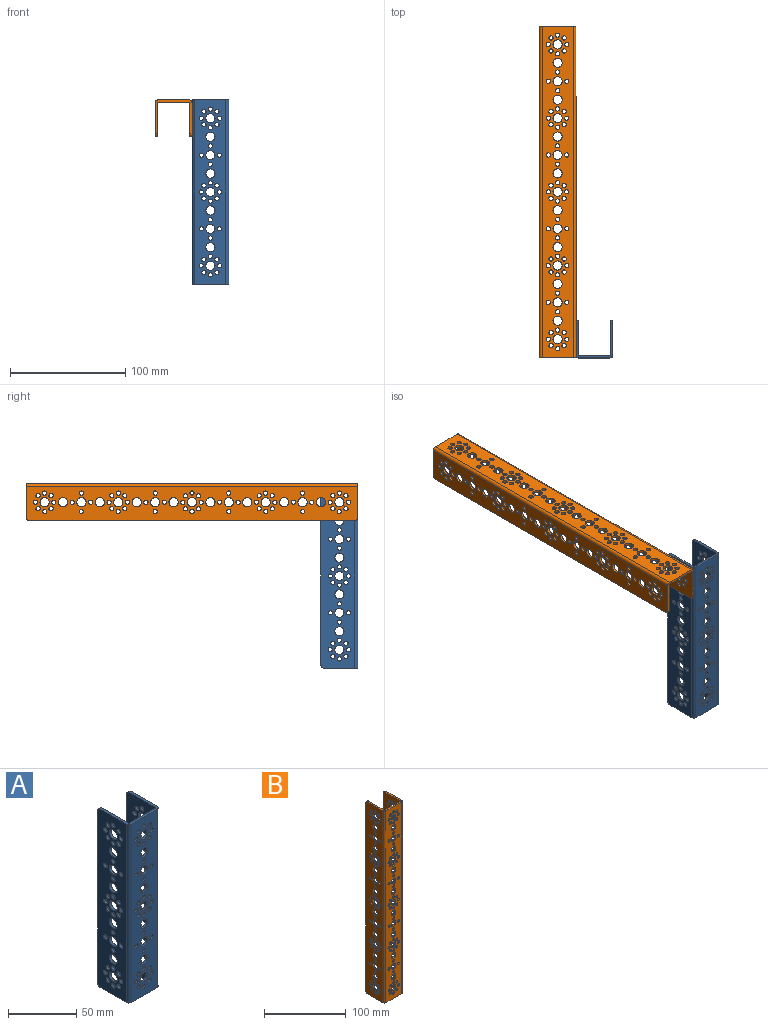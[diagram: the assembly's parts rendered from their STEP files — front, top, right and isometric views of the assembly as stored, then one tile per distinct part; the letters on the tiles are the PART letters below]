
ASSEMBLY  parts=2 mates=1
PART A: 141 faces, bbox 32x32x160 mm
  f0: cylinder r=2.5mm len=160mm, axis (0,0,-1), area 628.3mm2, adj f1,f11,f12,f13
  f1: plane 160x27mm, normal (0,-1,0), area 3523.5mm2, adj f0,f2,f12,f13,f18,f23,f24,f25
  f2: cylinder r=2.5mm len=160mm, axis (0,0,-1), area 628.3mm2, adj f1,f3,f12,f13
  f3: plane 160x29.5mm, normal (1,0,0), area 3920.9mm2, adj f2,f4,f12,f13,f14,f17,f20,f22
  f4: plane 155x2mm, normal (0,1,0), area 310mm2, adj f3,f5,f14,f17
  f5: plane 160x29.5mm, normal (-1,0,0), area 3920.9mm2, adj f4,f6,f12,f13,f14,f17,f20,f22
  f6: cylinder r=0.5mm len=160mm, axis (0,0,-1), area 125.7mm2, adj f5,f7,f12,f13
  f7: plane 160x27mm, normal (0,1,0), area 3523.5mm2, adj f6,f8,f12,f13,f18,f23,f24,f25
  f8: cylinder r=0.5mm len=160mm, axis (0,0,-1), area 125.7mm2, adj f7,f9,f12,f13
  f9: plane 160x29.5mm, normal (1,0,0), area 3920.9mm2, adj f8,f10,f12,f13,f15,f16,f19,f21
  f10: plane 155x2mm, normal (0,1,0), area 310mm2, adj f9,f11,f15,f16
  f11: plane 160x29.5mm, normal (-1,0,0), area 3920.9mm2, adj f0,f10,f12,f13,f15,f16,f19,f21
  f12: plane 32x29.5mm, normal (0,0,1), area 171.4mm2, adj f0,f1,f2,f3,f5,f6,f7,f8
  f13: plane 32x29.5mm, normal (0,0,-1), area 171.4mm2, adj f0,f1,f2,f3,f5,f6,f7,f8
  f14: cylinder r=2.5mm len=2.5mm, axis (1,0,0), area 7.9mm2, adj f3,f4,f5,f12
  f15: cylinder r=2.5mm len=2.5mm, axis (1,0,0), area 7.9mm2, adj f9,f10,f11,f12
  f16: cylinder r=2.5mm len=2.5mm, axis (-1,0,0), area 7.9mm2, adj f9,f10,f11,f13
  f17: cylinder r=2.5mm len=2.5mm, axis (-1,0,0), area 7.9mm2, adj f3,f4,f5,f13
  f18: cylinder r=4mm len=8mm, axis (0,-1,0), area 50.3mm2, adj f1,f7
  f19: cylinder r=4mm len=8mm, axis (-1,0,0), area 50.3mm2, adj f9,f11
  f20: cylinder r=4mm len=8mm, axis (-1,0,0), area 50.3mm2, adj f3,f5
  f21: cylinder r=1.85mm len=3.7mm, axis (-1,0,0), area 23.2mm2, adj f9,f11
  f22: cylinder r=1.85mm len=3.7mm, axis (-1,0,0), area 23.2mm2, adj f3,f5
  f23: cylinder r=1.85mm len=3.7mm, axis (0,-1,0), area 23.2mm2, adj f1,f7
  f24: cylinder r=4mm len=8mm, axis (0,-1,0), area 50.3mm2, adj f1,f7
  f25: cylinder r=4mm len=8mm, axis (0,-1,0), area 50.3mm2, adj f1,f7
  f26: cylinder r=4mm len=8mm, axis (0,-1,0), area 50.3mm2, adj f1,f7
  f27: cylinder r=4mm len=8mm, axis (0,-1,0), area 50.3mm2, adj f1,f7
  f28: cylinder r=4mm len=8mm, axis (0,-1,0), area 50.3mm2, adj f1,f7
  f29: cylinder r=4mm len=8mm, axis (0,-1,0), area 50.3mm2, adj f1,f7
  f30: cylinder r=4mm len=8mm, axis (0,-1,0), area 50.3mm2, adj f1,f7
  f31: cylinder r=4mm len=8mm, axis (0,-1,0), area 50.3mm2, adj f1,f7
  f32: cylinder r=4mm len=8mm, axis (-1,0,0), area 50.3mm2, adj f9,f11
  f33: cylinder r=4mm len=8mm, axis (-1,0,0), area 50.3mm2, adj f3,f5
  f34: cylinder r=4mm len=8mm, axis (-1,0,0), area 50.3mm2, adj f9,f11
  f35: cylinder r=4mm len=8mm, axis (-1,0,0), area 50.3mm2, adj f3,f5
  f36: cylinder r=4mm len=8mm, axis (-1,0,0), area 50.3mm2, adj f9,f11
  f37: cylinder r=4mm len=8mm, axis (-1,0,0), area 50.3mm2, adj f3,f5
  f38: cylinder r=4mm len=8mm, axis (-1,0,0), area 50.3mm2, adj f9,f11
  f39: cylinder r=4mm len=8mm, axis (-1,0,0), area 50.3mm2, adj f3,f5
  f40: cylinder r=4mm len=8mm, axis (-1,0,0), area 50.3mm2, adj f9,f11
  f41: cylinder r=4mm len=8mm, axis (-1,0,0), area 50.3mm2, adj f3,f5
  f42: cylinder r=4mm len=8mm, axis (-1,0,0), area 50.3mm2, adj f9,f11
  f43: cylinder r=4mm len=8mm, axis (-1,0,0), area 50.3mm2, adj f3,f5
  f44: cylinder r=4mm len=8mm, axis (-1,0,0), area 50.3mm2, adj f9,f11
  f45: cylinder r=4mm len=8mm, axis (-1,0,0), area 50.3mm2, adj f3,f5
  f46: cylinder r=4mm len=8mm, axis (-1,0,0), area 50.3mm2, adj f9,f11
  f47: cylinder r=4mm len=8mm, axis (-1,0,0), area 50.3mm2, adj f3,f5
  f48: cylinder r=1.85mm len=3.7mm, axis (0,-1,0), area 23.2mm2, adj f1,f7
  f49: cylinder r=1.85mm len=3.7mm, axis (0,-1,0), area 23.2mm2, adj f1,f7
  f50: cylinder r=1.85mm len=3.7mm, axis (0,-1,0), area 23.2mm2, adj f1,f7
  f51: cylinder r=1.85mm len=3.7mm, axis (0,-1,0), area 23.2mm2, adj f1,f7
  f52: cylinder r=1.85mm len=3.7mm, axis (0,-1,0), area 23.2mm2, adj f1,f7
  f53: cylinder r=1.85mm len=3.7mm, axis (0,-1,0), area 23.2mm2, adj f1,f7
  f54: cylinder r=1.85mm len=3.7mm, axis (0,-1,0), area 23.2mm2, adj f1,f7
  f55: cylinder r=1.85mm len=3.7mm, axis (-1,0,0), area 23.2mm2, adj f9,f11
  f56: cylinder r=1.85mm len=3.7mm, axis (-1,0,0), area 23.2mm2, adj f3,f5
  f57: cylinder r=1.85mm len=3.7mm, axis (-1,0,0), area 23.2mm2, adj f9,f11
  f58: cylinder r=1.85mm len=3.7mm, axis (-1,0,0), area 23.2mm2, adj f3,f5
  f59: cylinder r=1.85mm len=3.7mm, axis (-1,0,0), area 23.2mm2, adj f9,f11
  f60: cylinder r=1.85mm len=3.7mm, axis (-1,0,0), area 23.2mm2, adj f3,f5
  f61: cylinder r=1.85mm len=3.7mm, axis (-1,0,0), area 23.2mm2, adj f9,f11
  f62: cylinder r=1.85mm len=3.7mm, axis (-1,0,0), area 23.2mm2, adj f3,f5
  f63: cylinder r=1.85mm len=3.7mm, axis (-1,0,0), area 23.2mm2, adj f9,f11
  f64: cylinder r=1.85mm len=3.7mm, axis (-1,0,0), area 23.2mm2, adj f3,f5
  f65: cylinder r=1.85mm len=3.7mm, axis (-1,0,0), area 23.2mm2, adj f9,f11
  f66: cylinder r=1.85mm len=3.7mm, axis (-1,0,0), area 23.2mm2, adj f3,f5
  f67: cylinder r=1.85mm len=3.7mm, axis (-1,0,0), area 23.2mm2, adj f9,f11
  f68: cylinder r=1.85mm len=3.7mm, axis (-1,0,0), area 23.2mm2, adj f3,f5
  f69: cylinder r=1.85mm len=3.7mm, axis (0,-1,0), area 23.2mm2, adj f1,f7
  f70: cylinder r=1.85mm len=3.7mm, axis (-1,0,0), area 23.2mm2, adj f9,f11
  f71: cylinder r=1.85mm len=3.7mm, axis (-1,0,0), area 23.2mm2, adj f3,f5
  f72: cylinder r=1.85mm len=3.7mm, axis (0,-1,0), area 23.2mm2, adj f1,f7
  f73: cylinder r=1.85mm len=3.7mm, axis (0,-1,0), area 23.2mm2, adj f1,f7
  f74: cylinder r=1.85mm len=3.7mm, axis (0,-1,0), area 23.2mm2, adj f1,f7
  f75: cylinder r=1.85mm len=3.7mm, axis (-1,0,0), area 23.2mm2, adj f9,f11
  f76: cylinder r=1.85mm len=3.7mm, axis (-1,0,0), area 23.2mm2, adj f3,f5
  f77: cylinder r=1.85mm len=3.7mm, axis (-1,0,0), area 23.2mm2, adj f9,f11
  f78: cylinder r=1.85mm len=3.7mm, axis (-1,0,0), area 23.2mm2, adj f3,f5
  f79: cylinder r=1.85mm len=3.7mm, axis (-1,0,0), area 23.2mm2, adj f9,f11
  f80: cylinder r=1.85mm len=3.7mm, axis (-1,0,0), area 23.2mm2, adj f3,f5
  f81: cylinder r=1.85mm len=3.7mm, axis (0,-1,0), area 23.2mm2, adj f1,f7
  f82: cylinder r=1.85mm len=3.7mm, axis (0,-1,0), area 23.2mm2, adj f1,f7
  f83: cylinder r=1.85mm len=3.7mm, axis (0,-1,0), area 23.2mm2, adj f1,f7
  f84: cylinder r=1.85mm len=3.7mm, axis (0,-1,0), area 23.2mm2, adj f1,f7
  f85: cylinder r=1.85mm len=3.7mm, axis (0,-1,0), area 23.2mm2, adj f1,f7
  f86: cylinder r=1.85mm len=3.7mm, axis (0,-1,0), area 23.2mm2, adj f1,f7
  f87: cylinder r=1.85mm len=3.7mm, axis (0,-1,0), area 23.2mm2, adj f1,f7
  f88: cylinder r=1.85mm len=3.7mm, axis (0,-1,0), area 23.2mm2, adj f1,f7
  f89: cylinder r=1.85mm len=3.7mm, axis (-1,0,0), area 23.2mm2, adj f9,f11
  f90: cylinder r=1.85mm len=3.7mm, axis (-1,0,0), area 23.2mm2, adj f3,f5
  f91: cylinder r=1.85mm len=3.7mm, axis (-1,0,0), area 23.2mm2, adj f9,f11
  f92: cylinder r=1.85mm len=3.7mm, axis (-1,0,0), area 23.2mm2, adj f3,f5
  f93: cylinder r=1.85mm len=3.7mm, axis (-1,0,0), area 23.2mm2, adj f9,f11
  f94: cylinder r=1.85mm len=3.7mm, axis (-1,0,0), area 23.2mm2, adj f3,f5
  f95: cylinder r=1.85mm len=3.7mm, axis (-1,0,0), area 23.2mm2, adj f9,f11
  f96: cylinder r=1.85mm len=3.7mm, axis (-1,0,0), area 23.2mm2, adj f3,f5
  f97: cylinder r=1.85mm len=3.7mm, axis (-1,0,0), area 23.2mm2, adj f9,f11
  f98: cylinder r=1.85mm len=3.7mm, axis (-1,0,0), area 23.2mm2, adj f3,f5
  f99: cylinder r=1.85mm len=3.7mm, axis (-1,0,0), area 23.2mm2, adj f9,f11
  f100: cylinder r=1.85mm len=3.7mm, axis (-1,0,0), area 23.2mm2, adj f3,f5
  f101: cylinder r=1.85mm len=3.7mm, axis (-1,0,0), area 23.2mm2, adj f9,f11
  f102: cylinder r=1.85mm len=3.7mm, axis (-1,0,0), area 23.2mm2, adj f3,f5
  f103: cylinder r=1.85mm len=3.7mm, axis (-1,0,0), area 23.2mm2, adj f9,f11
  f104: cylinder r=1.85mm len=3.7mm, axis (-1,0,0), area 23.2mm2, adj f3,f5
  f105: cylinder r=1.85mm len=3.7mm, axis (0,-1,0), area 23.2mm2, adj f1,f7
  f106: cylinder r=1.85mm len=3.7mm, axis (0,-1,0), area 23.2mm2, adj f1,f7
  f107: cylinder r=1.85mm len=3.7mm, axis (0,-1,0), area 23.2mm2, adj f1,f7
  f108: cylinder r=1.85mm len=3.7mm, axis (0,-1,0), area 23.2mm2, adj f1,f7
  f109: cylinder r=1.85mm len=3.7mm, axis (-1,0,0), area 23.2mm2, adj f3,f5
  f110: cylinder r=1.85mm len=3.7mm, axis (-1,0,0), area 23.2mm2, adj f3,f5
  f111: cylinder r=1.85mm len=3.7mm, axis (-1,0,0), area 23.2mm2, adj f3,f5
  f112: cylinder r=1.85mm len=3.7mm, axis (-1,0,0), area 23.2mm2, adj f3,f5
  f113: cylinder r=1.85mm len=3.7mm, axis (-1,0,0), area 23.2mm2, adj f9,f11
  f114: cylinder r=1.85mm len=3.7mm, axis (-1,0,0), area 23.2mm2, adj f9,f11
  f115: cylinder r=1.85mm len=3.7mm, axis (-1,0,0), area 23.2mm2, adj f9,f11
  f116: cylinder r=1.85mm len=3.7mm, axis (-1,0,0), area 23.2mm2, adj f9,f11
  f117: cylinder r=1.85mm len=3.7mm, axis (-1,0,0), area 23.2mm2, adj f3,f5
  f118: cylinder r=1.85mm len=3.7mm, axis (-1,0,0), area 23.2mm2, adj f3,f5
  f119: cylinder r=1.85mm len=3.7mm, axis (-1,0,0), area 23.2mm2, adj f3,f5
  f120: cylinder r=1.85mm len=3.7mm, axis (-1,0,0), area 23.2mm2, adj f3,f5
  f121: cylinder r=1.85mm len=3.7mm, axis (-1,0,0), area 23.2mm2, adj f3,f5
  f122: cylinder r=1.85mm len=3.7mm, axis (-1,0,0), area 23.2mm2, adj f3,f5
  f123: cylinder r=1.85mm len=3.7mm, axis (-1,0,0), area 23.2mm2, adj f3,f5
  f124: cylinder r=1.85mm len=3.7mm, axis (-1,0,0), area 23.2mm2, adj f3,f5
  f125: cylinder r=1.85mm len=3.7mm, axis (-1,0,0), area 23.2mm2, adj f9,f11
  f126: cylinder r=1.85mm len=3.7mm, axis (-1,0,0), area 23.2mm2, adj f9,f11
  f127: cylinder r=1.85mm len=3.7mm, axis (-1,0,0), area 23.2mm2, adj f9,f11
  f128: cylinder r=1.85mm len=3.7mm, axis (-1,0,0), area 23.2mm2, adj f9,f11
  f129: cylinder r=1.85mm len=3.7mm, axis (-1,0,0), area 23.2mm2, adj f9,f11
  f130: cylinder r=1.85mm len=3.7mm, axis (-1,0,0), area 23.2mm2, adj f9,f11
  f131: cylinder r=1.85mm len=3.7mm, axis (-1,0,0), area 23.2mm2, adj f9,f11
  f132: cylinder r=1.85mm len=3.7mm, axis (-1,0,0), area 23.2mm2, adj f9,f11
  f133: cylinder r=1.85mm len=3.7mm, axis (0,-1,0), area 23.2mm2, adj f1,f7
  f134: cylinder r=1.85mm len=3.7mm, axis (0,-1,0), area 23.2mm2, adj f1,f7
  f135: cylinder r=1.85mm len=3.7mm, axis (0,-1,0), area 23.2mm2, adj f1,f7
  f136: cylinder r=1.85mm len=3.7mm, axis (0,-1,0), area 23.2mm2, adj f1,f7
  f137: cylinder r=1.85mm len=3.7mm, axis (0,-1,0), area 23.2mm2, adj f1,f7
  f138: cylinder r=1.85mm len=3.7mm, axis (0,-1,0), area 23.2mm2, adj f1,f7
  f139: cylinder r=1.85mm len=3.7mm, axis (0,-1,0), area 23.2mm2, adj f1,f7
  f140: cylinder r=1.85mm len=3.7mm, axis (0,-1,0), area 23.2mm2, adj f1,f7
PART B: 237 faces, bbox 32x32x288 mm
  f0: plane 288x29.5mm, normal (1,0,0), area 7036.7mm2, adj f7,f8,f12,f13,f14,f17,f20,f22
  f1: plane 288x29.5mm, normal (-1,0,0), area 7036.7mm2, adj f8,f9,f12,f13,f14,f17,f20,f22
  f2: plane 288x29.5mm, normal (1,0,0), area 7036.7mm2, adj f10,f11,f12,f13,f15,f16,f19,f21
  f3: plane 288x29.5mm, normal (-1,0,0), area 7036.7mm2, adj f6,f11,f12,f13,f15,f16,f19,f21
  f4: plane 288x27mm, normal (0,-1,0), area 6319.4mm2, adj f6,f7,f12,f13,f18,f23,f24,f25
  f5: plane 288x27mm, normal (0,1,0), area 6319.4mm2, adj f9,f10,f12,f13,f18,f23,f24,f25
  f6: cylinder r=2.5mm len=288mm, axis (0,0,-1), area 1131mm2, adj f3,f4,f12,f13
  f7: cylinder r=2.5mm len=288mm, axis (0,0,-1), area 1131mm2, adj f0,f4,f12,f13
  f8: plane 283x2mm, normal (0,1,0), area 566mm2, adj f0,f1,f14,f17
  f9: cylinder r=0.5mm len=288mm, axis (0,0,-1), area 226.2mm2, adj f1,f5,f12,f13
  f10: cylinder r=0.5mm len=288mm, axis (0,0,-1), area 226.2mm2, adj f2,f5,f12,f13
  f11: plane 283x2mm, normal (0,1,0), area 566mm2, adj f2,f3,f15,f16
  f12: plane 32x29.5mm, normal (0,0,1), area 171.4mm2, adj f0,f1,f2,f3,f4,f5,f6,f7
  f13: plane 32x29.5mm, normal (0,0,-1), area 171.4mm2, adj f0,f1,f2,f3,f4,f5,f6,f7
  f14: cylinder r=2.5mm len=2.5mm, axis (1,0,0), area 7.9mm2, adj f0,f1,f8,f12
  f15: cylinder r=2.5mm len=2.5mm, axis (1,0,0), area 7.9mm2, adj f2,f3,f11,f12
  f16: cylinder r=2.5mm len=2.5mm, axis (-1,0,0), area 7.9mm2, adj f2,f3,f11,f13
  f17: cylinder r=2.5mm len=2.5mm, axis (-1,0,0), area 7.9mm2, adj f0,f1,f8,f13
  f18: cylinder r=4mm len=8mm, axis (0,-1,0), area 50.3mm2, adj f4,f5
  f19: cylinder r=4mm len=8mm, axis (-1,0,0), area 50.3mm2, adj f2,f3
  f20: cylinder r=4mm len=8mm, axis (-1,0,0), area 50.3mm2, adj f0,f1
  f21: cylinder r=1.85mm len=3.7mm, axis (-1,0,0), area 23.2mm2, adj f2,f3
  f22: cylinder r=1.85mm len=3.7mm, axis (-1,0,0), area 23.2mm2, adj f0,f1
  f23: cylinder r=1.85mm len=3.7mm, axis (0,-1,0), area 23.2mm2, adj f4,f5
  f24: cylinder r=4mm len=8mm, axis (0,-1,0), area 50.3mm2, adj f4,f5
  f25: cylinder r=4mm len=8mm, axis (0,-1,0), area 50.3mm2, adj f4,f5
  f26: cylinder r=4mm len=8mm, axis (0,-1,0), area 50.3mm2, adj f4,f5
  f27: cylinder r=4mm len=8mm, axis (0,-1,0), area 50.3mm2, adj f4,f5
  f28: cylinder r=4mm len=8mm, axis (0,-1,0), area 50.3mm2, adj f4,f5
  f29: cylinder r=4mm len=8mm, axis (0,-1,0), area 50.3mm2, adj f4,f5
  f30: cylinder r=4mm len=8mm, axis (0,-1,0), area 50.3mm2, adj f4,f5
  f31: cylinder r=4mm len=8mm, axis (0,-1,0), area 50.3mm2, adj f4,f5
  f32: cylinder r=4mm len=8mm, axis (0,-1,0), area 50.3mm2, adj f4,f5
  f33: cylinder r=4mm len=8mm, axis (0,-1,0), area 50.3mm2, adj f4,f5
  f34: cylinder r=4mm len=8mm, axis (0,-1,0), area 50.3mm2, adj f4,f5
  f35: cylinder r=4mm len=8mm, axis (0,-1,0), area 50.3mm2, adj f4,f5
  f36: cylinder r=4mm len=8mm, axis (0,-1,0), area 50.3mm2, adj f4,f5
  f37: cylinder r=4mm len=8mm, axis (0,-1,0), area 50.3mm2, adj f4,f5
  f38: cylinder r=4mm len=8mm, axis (0,-1,0), area 50.3mm2, adj f4,f5
  f39: cylinder r=4mm len=8mm, axis (0,-1,0), area 50.3mm2, adj f4,f5
  f40: cylinder r=4mm len=8mm, axis (-1,0,0), area 50.3mm2, adj f2,f3
  f41: cylinder r=4mm len=8mm, axis (-1,0,0), area 50.3mm2, adj f0,f1
  f42: cylinder r=4mm len=8mm, axis (-1,0,0), area 50.3mm2, adj f2,f3
  f43: cylinder r=4mm len=8mm, axis (-1,0,0), area 50.3mm2, adj f0,f1
  f44: cylinder r=4mm len=8mm, axis (-1,0,0), area 50.3mm2, adj f2,f3
  f45: cylinder r=4mm len=8mm, axis (-1,0,0), area 50.3mm2, adj f0,f1
  f46: cylinder r=4mm len=8mm, axis (-1,0,0), area 50.3mm2, adj f2,f3
  f47: cylinder r=4mm len=8mm, axis (-1,0,0), area 50.3mm2, adj f0,f1
  f48: cylinder r=4mm len=8mm, axis (-1,0,0), area 50.3mm2, adj f2,f3
  f49: cylinder r=4mm len=8mm, axis (-1,0,0), area 50.3mm2, adj f0,f1
  f50: cylinder r=4mm len=8mm, axis (-1,0,0), area 50.3mm2, adj f2,f3
  f51: cylinder r=4mm len=8mm, axis (-1,0,0), area 50.3mm2, adj f0,f1
  f52: cylinder r=4mm len=8mm, axis (-1,0,0), area 50.3mm2, adj f2,f3
  f53: cylinder r=4mm len=8mm, axis (-1,0,0), area 50.3mm2, adj f0,f1
  f54: cylinder r=4mm len=8mm, axis (-1,0,0), area 50.3mm2, adj f2,f3
  f55: cylinder r=4mm len=8mm, axis (-1,0,0), area 50.3mm2, adj f0,f1
  f56: cylinder r=4mm len=8mm, axis (-1,0,0), area 50.3mm2, adj f2,f3
  f57: cylinder r=4mm len=8mm, axis (-1,0,0), area 50.3mm2, adj f0,f1
  f58: cylinder r=4mm len=8mm, axis (-1,0,0), area 50.3mm2, adj f2,f3
  f59: cylinder r=4mm len=8mm, axis (-1,0,0), area 50.3mm2, adj f0,f1
  f60: cylinder r=4mm len=8mm, axis (-1,0,0), area 50.3mm2, adj f2,f3
  f61: cylinder r=4mm len=8mm, axis (-1,0,0), area 50.3mm2, adj f0,f1
  f62: cylinder r=4mm len=8mm, axis (-1,0,0), area 50.3mm2, adj f2,f3
  f63: cylinder r=4mm len=8mm, axis (-1,0,0), area 50.3mm2, adj f0,f1
  f64: cylinder r=4mm len=8mm, axis (-1,0,0), area 50.3mm2, adj f2,f3
  f65: cylinder r=4mm len=8mm, axis (-1,0,0), area 50.3mm2, adj f0,f1
  f66: cylinder r=4mm len=8mm, axis (-1,0,0), area 50.3mm2, adj f2,f3
  f67: cylinder r=4mm len=8mm, axis (-1,0,0), area 50.3mm2, adj f0,f1
  f68: cylinder r=4mm len=8mm, axis (-1,0,0), area 50.3mm2, adj f2,f3
  f69: cylinder r=4mm len=8mm, axis (-1,0,0), area 50.3mm2, adj f0,f1
  f70: cylinder r=4mm len=8mm, axis (-1,0,0), area 50.3mm2, adj f2,f3
  f71: cylinder r=4mm len=8mm, axis (-1,0,0), area 50.3mm2, adj f0,f1
  f72: cylinder r=1.85mm len=3.7mm, axis (0,-1,0), area 23.2mm2, adj f4,f5
  f73: cylinder r=1.85mm len=3.7mm, axis (0,-1,0), area 23.2mm2, adj f4,f5
  f74: cylinder r=1.85mm len=3.7mm, axis (0,-1,0), area 23.2mm2, adj f4,f5
  f75: cylinder r=1.85mm len=3.7mm, axis (0,-1,0), area 23.2mm2, adj f4,f5
  f76: cylinder r=1.85mm len=3.7mm, axis (0,-1,0), area 23.2mm2, adj f4,f5
  f77: cylinder r=1.85mm len=3.7mm, axis (0,-1,0), area 23.2mm2, adj f4,f5
  f78: cylinder r=1.85mm len=3.7mm, axis (0,-1,0), area 23.2mm2, adj f4,f5
  f79: cylinder r=1.85mm len=3.7mm, axis (-1,0,0), area 23.2mm2, adj f2,f3
  f80: cylinder r=1.85mm len=3.7mm, axis (-1,0,0), area 23.2mm2, adj f0,f1
  f81: cylinder r=1.85mm len=3.7mm, axis (-1,0,0), area 23.2mm2, adj f2,f3
  f82: cylinder r=1.85mm len=3.7mm, axis (-1,0,0), area 23.2mm2, adj f0,f1
  f83: cylinder r=1.85mm len=3.7mm, axis (-1,0,0), area 23.2mm2, adj f2,f3
  f84: cylinder r=1.85mm len=3.7mm, axis (-1,0,0), area 23.2mm2, adj f0,f1
  f85: cylinder r=1.85mm len=3.7mm, axis (-1,0,0), area 23.2mm2, adj f2,f3
  f86: cylinder r=1.85mm len=3.7mm, axis (-1,0,0), area 23.2mm2, adj f0,f1
  f87: cylinder r=1.85mm len=3.7mm, axis (-1,0,0), area 23.2mm2, adj f2,f3
  f88: cylinder r=1.85mm len=3.7mm, axis (-1,0,0), area 23.2mm2, adj f0,f1
  f89: cylinder r=1.85mm len=3.7mm, axis (-1,0,0), area 23.2mm2, adj f2,f3
  f90: cylinder r=1.85mm len=3.7mm, axis (-1,0,0), area 23.2mm2, adj f0,f1
  f91: cylinder r=1.85mm len=3.7mm, axis (-1,0,0), area 23.2mm2, adj f2,f3
  f92: cylinder r=1.85mm len=3.7mm, axis (-1,0,0), area 23.2mm2, adj f0,f1
  f93: cylinder r=1.85mm len=3.7mm, axis (0,-1,0), area 23.2mm2, adj f4,f5
  f94: cylinder r=1.85mm len=3.7mm, axis (-1,0,0), area 23.2mm2, adj f2,f3
  f95: cylinder r=1.85mm len=3.7mm, axis (-1,0,0), area 23.2mm2, adj f0,f1
  f96: cylinder r=1.85mm len=3.7mm, axis (0,-1,0), area 23.2mm2, adj f4,f5
  f97: cylinder r=1.85mm len=3.7mm, axis (0,-1,0), area 23.2mm2, adj f4,f5
  f98: cylinder r=1.85mm len=3.7mm, axis (0,-1,0), area 23.2mm2, adj f4,f5
  f99: cylinder r=1.85mm len=3.7mm, axis (-1,0,0), area 23.2mm2, adj f2,f3
  f100: cylinder r=1.85mm len=3.7mm, axis (-1,0,0), area 23.2mm2, adj f0,f1
  f101: cylinder r=1.85mm len=3.7mm, axis (-1,0,0), area 23.2mm2, adj f2,f3
  f102: cylinder r=1.85mm len=3.7mm, axis (-1,0,0), area 23.2mm2, adj f0,f1
  f103: cylinder r=1.85mm len=3.7mm, axis (-1,0,0), area 23.2mm2, adj f2,f3
  f104: cylinder r=1.85mm len=3.7mm, axis (-1,0,0), area 23.2mm2, adj f0,f1
  f105: cylinder r=1.85mm len=3.7mm, axis (0,-1,0), area 23.2mm2, adj f4,f5
  f106: cylinder r=1.85mm len=3.7mm, axis (0,-1,0), area 23.2mm2, adj f4,f5
  f107: cylinder r=1.85mm len=3.7mm, axis (0,-1,0), area 23.2mm2, adj f4,f5
  f108: cylinder r=1.85mm len=3.7mm, axis (0,-1,0), area 23.2mm2, adj f4,f5
  f109: cylinder r=1.85mm len=3.7mm, axis (0,-1,0), area 23.2mm2, adj f4,f5
  f110: cylinder r=1.85mm len=3.7mm, axis (0,-1,0), area 23.2mm2, adj f4,f5
  f111: cylinder r=1.85mm len=3.7mm, axis (0,-1,0), area 23.2mm2, adj f4,f5
  f112: cylinder r=1.85mm len=3.7mm, axis (0,-1,0), area 23.2mm2, adj f4,f5
  f113: cylinder r=1.85mm len=3.7mm, axis (0,-1,0), area 23.2mm2, adj f4,f5
  f114: cylinder r=1.85mm len=3.7mm, axis (0,-1,0), area 23.2mm2, adj f4,f5
  f115: cylinder r=1.85mm len=3.7mm, axis (0,-1,0), area 23.2mm2, adj f4,f5
  f116: cylinder r=1.85mm len=3.7mm, axis (0,-1,0), area 23.2mm2, adj f4,f5
  f117: cylinder r=1.85mm len=3.7mm, axis (0,-1,0), area 23.2mm2, adj f4,f5
  f118: cylinder r=1.85mm len=3.7mm, axis (0,-1,0), area 23.2mm2, adj f4,f5
  f119: cylinder r=1.85mm len=3.7mm, axis (0,-1,0), area 23.2mm2, adj f4,f5
  f120: cylinder r=1.85mm len=3.7mm, axis (0,-1,0), area 23.2mm2, adj f4,f5
  f121: cylinder r=1.85mm len=3.7mm, axis (-1,0,0), area 23.2mm2, adj f2,f3
  f122: cylinder r=1.85mm len=3.7mm, axis (-1,0,0), area 23.2mm2, adj f0,f1
  f123: cylinder r=1.85mm len=3.7mm, axis (-1,0,0), area 23.2mm2, adj f2,f3
  f124: cylinder r=1.85mm len=3.7mm, axis (-1,0,0), area 23.2mm2, adj f0,f1
  f125: cylinder r=1.85mm len=3.7mm, axis (-1,0,0), area 23.2mm2, adj f2,f3
  f126: cylinder r=1.85mm len=3.7mm, axis (-1,0,0), area 23.2mm2, adj f0,f1
  f127: cylinder r=1.85mm len=3.7mm, axis (-1,0,0), area 23.2mm2, adj f2,f3
  f128: cylinder r=1.85mm len=3.7mm, axis (-1,0,0), area 23.2mm2, adj f0,f1
  f129: cylinder r=1.85mm len=3.7mm, axis (-1,0,0), area 23.2mm2, adj f2,f3
  f130: cylinder r=1.85mm len=3.7mm, axis (-1,0,0), area 23.2mm2, adj f0,f1
  f131: cylinder r=1.85mm len=3.7mm, axis (-1,0,0), area 23.2mm2, adj f2,f3
  f132: cylinder r=1.85mm len=3.7mm, axis (-1,0,0), area 23.2mm2, adj f0,f1
  f133: cylinder r=1.85mm len=3.7mm, axis (-1,0,0), area 23.2mm2, adj f2,f3
  f134: cylinder r=1.85mm len=3.7mm, axis (-1,0,0), area 23.2mm2, adj f0,f1
  f135: cylinder r=1.85mm len=3.7mm, axis (-1,0,0), area 23.2mm2, adj f2,f3
  f136: cylinder r=1.85mm len=3.7mm, axis (-1,0,0), area 23.2mm2, adj f0,f1
  f137: cylinder r=1.85mm len=3.7mm, axis (-1,0,0), area 23.2mm2, adj f2,f3
  f138: cylinder r=1.85mm len=3.7mm, axis (-1,0,0), area 23.2mm2, adj f0,f1
  f139: cylinder r=1.85mm len=3.7mm, axis (-1,0,0), area 23.2mm2, adj f2,f3
  f140: cylinder r=1.85mm len=3.7mm, axis (-1,0,0), area 23.2mm2, adj f0,f1
  f141: cylinder r=1.85mm len=3.7mm, axis (-1,0,0), area 23.2mm2, adj f2,f3
  f142: cylinder r=1.85mm len=3.7mm, axis (-1,0,0), area 23.2mm2, adj f0,f1
  f143: cylinder r=1.85mm len=3.7mm, axis (-1,0,0), area 23.2mm2, adj f2,f3
  f144: cylinder r=1.85mm len=3.7mm, axis (-1,0,0), area 23.2mm2, adj f0,f1
  f145: cylinder r=1.85mm len=3.7mm, axis (-1,0,0), area 23.2mm2, adj f2,f3
  f146: cylinder r=1.85mm len=3.7mm, axis (-1,0,0), area 23.2mm2, adj f0,f1
  f147: cylinder r=1.85mm len=3.7mm, axis (-1,0,0), area 23.2mm2, adj f2,f3
  f148: cylinder r=1.85mm len=3.7mm, axis (-1,0,0), area 23.2mm2, adj f0,f1
  f149: cylinder r=1.85mm len=3.7mm, axis (-1,0,0), area 23.2mm2, adj f2,f3
  f150: cylinder r=1.85mm len=3.7mm, axis (-1,0,0), area 23.2mm2, adj f0,f1
  f151: cylinder r=1.85mm len=3.7mm, axis (-1,0,0), area 23.2mm2, adj f2,f3
  f152: cylinder r=1.85mm len=3.7mm, axis (-1,0,0), area 23.2mm2, adj f0,f1
  f153: cylinder r=1.85mm len=3.7mm, axis (0,-1,0), area 23.2mm2, adj f4,f5
  f154: cylinder r=1.85mm len=3.7mm, axis (0,-1,0), area 23.2mm2, adj f4,f5
  f155: cylinder r=1.85mm len=3.7mm, axis (0,-1,0), area 23.2mm2, adj f4,f5
  f156: cylinder r=1.85mm len=3.7mm, axis (0,-1,0), area 23.2mm2, adj f4,f5
  f157: cylinder r=1.85mm len=3.7mm, axis (-1,0,0), area 23.2mm2, adj f2,f3
  f158: cylinder r=1.85mm len=3.7mm, axis (-1,0,0), area 23.2mm2, adj f0,f1
  f159: cylinder r=1.85mm len=3.7mm, axis (-1,0,0), area 23.2mm2, adj f2,f3
  f160: cylinder r=1.85mm len=3.7mm, axis (-1,0,0), area 23.2mm2, adj f0,f1
  f161: cylinder r=1.85mm len=3.7mm, axis (-1,0,0), area 23.2mm2, adj f2,f3
  f162: cylinder r=1.85mm len=3.7mm, axis (-1,0,0), area 23.2mm2, adj f0,f1
  f163: cylinder r=1.85mm len=3.7mm, axis (-1,0,0), area 23.2mm2, adj f2,f3
  f164: cylinder r=1.85mm len=3.7mm, axis (-1,0,0), area 23.2mm2, adj f0,f1
  f165: cylinder r=1.85mm len=3.7mm, axis (0,-1,0), area 23.2mm2, adj f4,f5
  f166: cylinder r=1.85mm len=3.7mm, axis (0,-1,0), area 23.2mm2, adj f4,f5
  f167: cylinder r=1.85mm len=3.7mm, axis (0,-1,0), area 23.2mm2, adj f4,f5
  f168: cylinder r=1.85mm len=3.7mm, axis (0,-1,0), area 23.2mm2, adj f4,f5
  f169: cylinder r=1.85mm len=3.7mm, axis (0,-1,0), area 23.2mm2, adj f4,f5
  f170: cylinder r=1.85mm len=3.7mm, axis (0,-1,0), area 23.2mm2, adj f4,f5
  f171: cylinder r=1.85mm len=3.7mm, axis (0,-1,0), area 23.2mm2, adj f4,f5
  f172: cylinder r=1.85mm len=3.7mm, axis (0,-1,0), area 23.2mm2, adj f4,f5
  f173: cylinder r=1.85mm len=3.7mm, axis (0,-1,0), area 23.2mm2, adj f4,f5
  f174: cylinder r=1.85mm len=3.7mm, axis (0,-1,0), area 23.2mm2, adj f4,f5
  f175: cylinder r=1.85mm len=3.7mm, axis (0,-1,0), area 23.2mm2, adj f4,f5
  f176: cylinder r=1.85mm len=3.7mm, axis (0,-1,0), area 23.2mm2, adj f4,f5
  f177: cylinder r=1.85mm len=3.7mm, axis (0,-1,0), area 23.2mm2, adj f4,f5
  f178: cylinder r=1.85mm len=3.7mm, axis (0,-1,0), area 23.2mm2, adj f4,f5
  f179: cylinder r=1.85mm len=3.7mm, axis (0,-1,0), area 23.2mm2, adj f4,f5
  f180: cylinder r=1.85mm len=3.7mm, axis (0,-1,0), area 23.2mm2, adj f4,f5
  f181: cylinder r=1.85mm len=3.7mm, axis (-1,0,0), area 23.2mm2, adj f2,f3
  f182: cylinder r=1.85mm len=3.7mm, axis (-1,0,0), area 23.2mm2, adj f0,f1
  f183: cylinder r=1.85mm len=3.7mm, axis (-1,0,0), area 23.2mm2, adj f2,f3
  f184: cylinder r=1.85mm len=3.7mm, axis (-1,0,0), area 23.2mm2, adj f0,f1
  f185: cylinder r=1.85mm len=3.7mm, axis (-1,0,0), area 23.2mm2, adj f2,f3
  f186: cylinder r=1.85mm len=3.7mm, axis (-1,0,0), area 23.2mm2, adj f0,f1
  f187: cylinder r=1.85mm len=3.7mm, axis (-1,0,0), area 23.2mm2, adj f2,f3
  f188: cylinder r=1.85mm len=3.7mm, axis (-1,0,0), area 23.2mm2, adj f0,f1
  f189: cylinder r=1.85mm len=3.7mm, axis (-1,0,0), area 23.2mm2, adj f2,f3
  f190: cylinder r=1.85mm len=3.7mm, axis (-1,0,0), area 23.2mm2, adj f0,f1
  f191: cylinder r=1.85mm len=3.7mm, axis (-1,0,0), area 23.2mm2, adj f2,f3
  f192: cylinder r=1.85mm len=3.7mm, axis (-1,0,0), area 23.2mm2, adj f0,f1
  f193: cylinder r=1.85mm len=3.7mm, axis (-1,0,0), area 23.2mm2, adj f2,f3
  f194: cylinder r=1.85mm len=3.7mm, axis (-1,0,0), area 23.2mm2, adj f0,f1
  f195: cylinder r=1.85mm len=3.7mm, axis (-1,0,0), area 23.2mm2, adj f2,f3
  f196: cylinder r=1.85mm len=3.7mm, axis (-1,0,0), area 23.2mm2, adj f0,f1
  f197: cylinder r=1.85mm len=3.7mm, axis (-1,0,0), area 23.2mm2, adj f2,f3
  f198: cylinder r=1.85mm len=3.7mm, axis (-1,0,0), area 23.2mm2, adj f0,f1
  f199: cylinder r=1.85mm len=3.7mm, axis (-1,0,0), area 23.2mm2, adj f2,f3
  f200: cylinder r=1.85mm len=3.7mm, axis (-1,0,0), area 23.2mm2, adj f0,f1
  f201: cylinder r=1.85mm len=3.7mm, axis (-1,0,0), area 23.2mm2, adj f2,f3
  f202: cylinder r=1.85mm len=3.7mm, axis (-1,0,0), area 23.2mm2, adj f0,f1
  f203: cylinder r=1.85mm len=3.7mm, axis (-1,0,0), area 23.2mm2, adj f2,f3
  f204: cylinder r=1.85mm len=3.7mm, axis (-1,0,0), area 23.2mm2, adj f0,f1
  f205: cylinder r=1.85mm len=3.7mm, axis (-1,0,0), area 23.2mm2, adj f2,f3
  f206: cylinder r=1.85mm len=3.7mm, axis (-1,0,0), area 23.2mm2, adj f0,f1
  f207: cylinder r=1.85mm len=3.7mm, axis (-1,0,0), area 23.2mm2, adj f2,f3
  f208: cylinder r=1.85mm len=3.7mm, axis (-1,0,0), area 23.2mm2, adj f0,f1
  f209: cylinder r=1.85mm len=3.7mm, axis (-1,0,0), area 23.2mm2, adj f2,f3
  f210: cylinder r=1.85mm len=3.7mm, axis (-1,0,0), area 23.2mm2, adj f0,f1
  f211: cylinder r=1.85mm len=3.7mm, axis (-1,0,0), area 23.2mm2, adj f2,f3
  f212: cylinder r=1.85mm len=3.7mm, axis (-1,0,0), area 23.2mm2, adj f0,f1
  f213: cylinder r=1.85mm len=3.7mm, axis (0,-1,0), area 23.2mm2, adj f4,f5
  f214: cylinder r=1.85mm len=3.7mm, axis (0,-1,0), area 23.2mm2, adj f4,f5
  f215: cylinder r=1.85mm len=3.7mm, axis (0,-1,0), area 23.2mm2, adj f4,f5
  f216: cylinder r=1.85mm len=3.7mm, axis (0,-1,0), area 23.2mm2, adj f4,f5
  f217: cylinder r=1.85mm len=3.7mm, axis (0,-1,0), area 23.2mm2, adj f4,f5
  f218: cylinder r=1.85mm len=3.7mm, axis (0,-1,0), area 23.2mm2, adj f4,f5
  f219: cylinder r=1.85mm len=3.7mm, axis (0,-1,0), area 23.2mm2, adj f4,f5
  f220: cylinder r=1.85mm len=3.7mm, axis (0,-1,0), area 23.2mm2, adj f4,f5
  f221: cylinder r=1.85mm len=3.7mm, axis (-1,0,0), area 23.2mm2, adj f2,f3
  f222: cylinder r=1.85mm len=3.7mm, axis (-1,0,0), area 23.2mm2, adj f0,f1
  f223: cylinder r=1.85mm len=3.7mm, axis (-1,0,0), area 23.2mm2, adj f2,f3
  f224: cylinder r=1.85mm len=3.7mm, axis (-1,0,0), area 23.2mm2, adj f0,f1
  f225: cylinder r=1.85mm len=3.7mm, axis (-1,0,0), area 23.2mm2, adj f2,f3
  f226: cylinder r=1.85mm len=3.7mm, axis (-1,0,0), area 23.2mm2, adj f0,f1
  f227: cylinder r=1.85mm len=3.7mm, axis (-1,0,0), area 23.2mm2, adj f2,f3
  f228: cylinder r=1.85mm len=3.7mm, axis (-1,0,0), area 23.2mm2, adj f0,f1
  f229: cylinder r=1.85mm len=3.7mm, axis (-1,0,0), area 23.2mm2, adj f2,f3
  f230: cylinder r=1.85mm len=3.7mm, axis (-1,0,0), area 23.2mm2, adj f0,f1
  f231: cylinder r=1.85mm len=3.7mm, axis (-1,0,0), area 23.2mm2, adj f2,f3
  f232: cylinder r=1.85mm len=3.7mm, axis (-1,0,0), area 23.2mm2, adj f0,f1
  f233: cylinder r=1.85mm len=3.7mm, axis (-1,0,0), area 23.2mm2, adj f2,f3
  f234: cylinder r=1.85mm len=3.7mm, axis (-1,0,0), area 23.2mm2, adj f0,f1
  f235: cylinder r=1.85mm len=3.7mm, axis (-1,0,0), area 23.2mm2, adj f2,f3
  f236: cylinder r=1.85mm len=3.7mm, axis (-1,0,0), area 23.2mm2, adj f0,f1
PLACE A t=(-0.72,-16.68,-0.41)mm fixed
PLACE B rot(axis=(0,-0.71,0.71),180deg) t=(-32.72,127.32,79.59)mm
MATE fastened A.f38 <-> B.f54  axis (-1,0,0) through (-16.72,-0.68,63.59)mm
